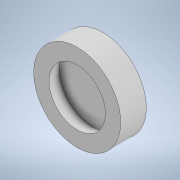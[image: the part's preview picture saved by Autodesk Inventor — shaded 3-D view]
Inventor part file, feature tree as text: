
AUTODESK INVENTOR PART (.ipt)
format: ipt  version: 2021 (Build 250183000, 183)  size: 109,056 bytes
history: native  units: in
note: dims shown in document units (in); Inventor stores cm internally (conversion verified against a paired STEP export)
features: revolve x1, extrude x1, sketch x1
ambient origin geometry x8: Origin, YZ Plane, XZ Plane, XY Plane, X Axis, Y Axis, Z Axis, Center Point
bodies: Body1 (feature_tree)
feature tree (3):
  revolve  "Revolution1"  Angle=90.0deg
  extrude  "Extrusion3"  Depth=0.0787in TaperAngle=0.0deg
  sketch  "Sketch3"  dims[d11=0.0787in d12=90.0deg d13=0.0787in d14=0.0in]
